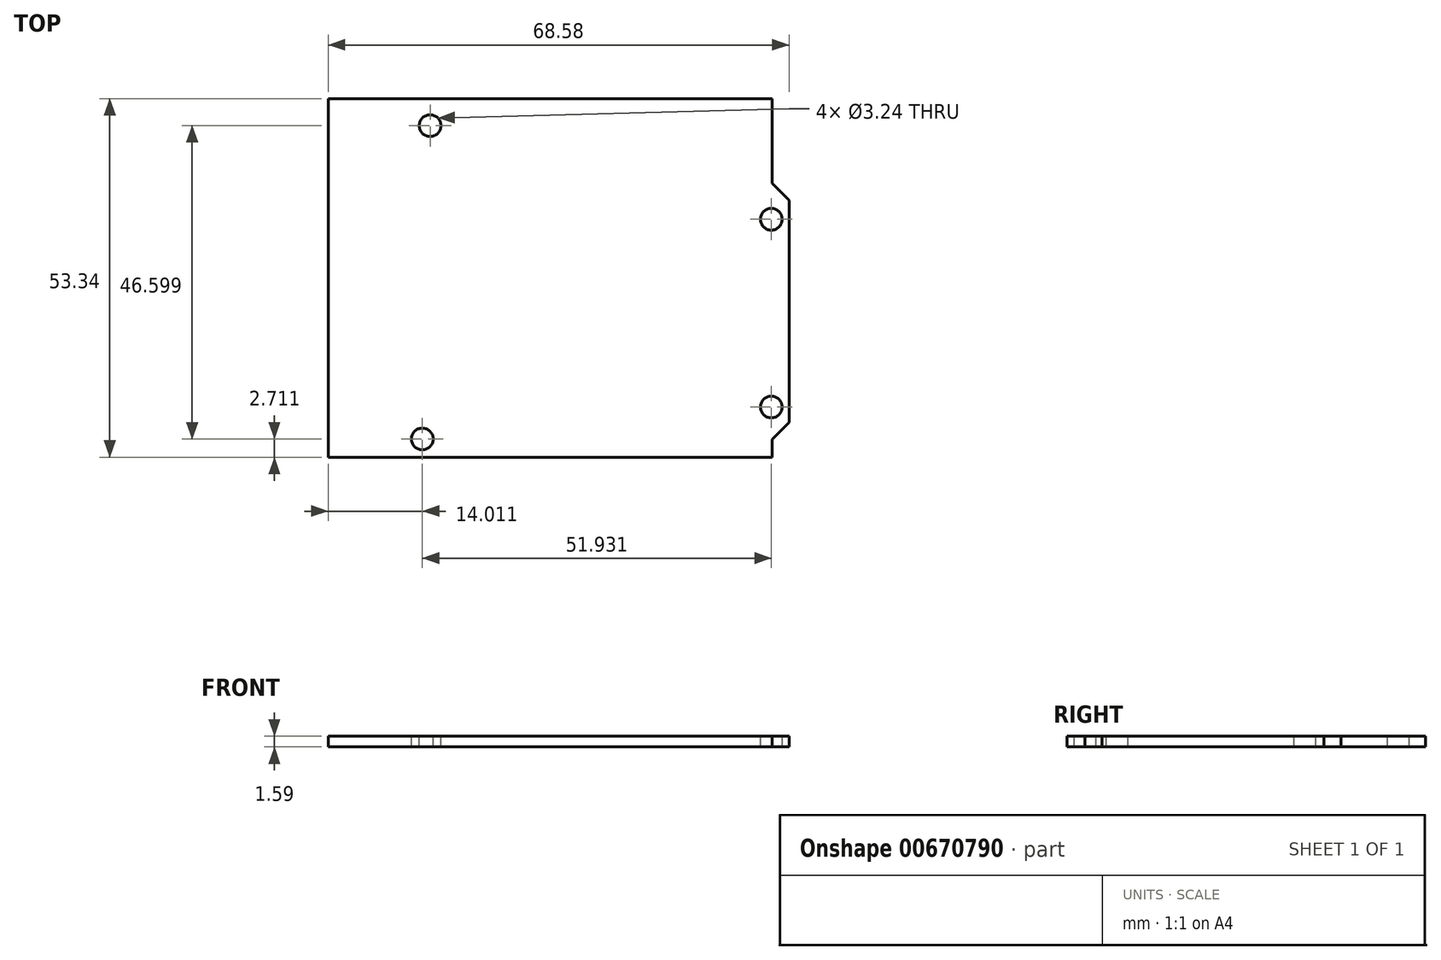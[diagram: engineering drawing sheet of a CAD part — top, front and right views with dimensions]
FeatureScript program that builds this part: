
annotation { "Feature Type Name" : "Feature", "Feature Type Description" : "" }
export const myFeature = defineFeature(function(context is Context, id is Id, definition is map)
    precondition{}
    {
        {
            var Q0;
            Q0=qCreatedBy(makeId("Top.planeOp"),FACE);
            var sketch = newSketch(context, id + "F0", { "sketchPlane" : qUnion([Q0])});
            skLineSegment(sketch, "E0", {"start": v(-34.46, 26.67) * mm, "end": v(-34.46, -26.67) * mm});
            skLineSegment(sketch, "E1", {"start": v(-34.46, -26.67) * mm, "end": v(31.58, -26.67) * mm});
            skLineSegment(sketch, "E2", {"start": v(31.58, -26.67) * mm, "end": v(31.58, 26.67) * mm});
            skLineSegment(sketch, "E3", {"start": v(31.58, 26.67) * mm, "end": v(-34.46, 26.67) * mm});
            skLineSegment(sketch, "E4", {"start": v(0, 26.67) * mm, "end": v(0, 0) * mm, "construction": true});
            skLineSegment(sketch, "E5", {"start": v(0, 0) * mm, "end": v(-34.46, 0) * mm, "construction": true});
            skLineSegment(sketch, "E6", {"start": v(31.58, -24) * mm, "end": v(34.12, -21.46) * mm});
            skLineSegment(sketch, "E7", {"start": v(34.12, -21.46) * mm, "end": v(34.12, 11.56) * mm});
            skLineSegment(sketch, "E8", {"start": v(34.12, 11.56) * mm, "end": v(31.58, 14.1) * mm});
            skSolve(sketch);
        }
        {
            var Q0;
            Q0 = qSketchRegion(id + "F0", true);
            extrude(context, id + "F1", {"entities" : qUnion([Q0]), "depth" : 1.59 * mm, "offsetDistance" : 25 * mm});
        }
        {
            var Q0;
            Q0=makeQuery(id+"F1.opExtrude","CAP_FACE",FACE,{"disambiguationData":[OSD([sQuery(id+"F0.wireOp",EDGE,"E0"),sQuery(id+"F0.wireOp",EDGE,"E1"),sQuery(id+"F0.wireOp",EDGE,"E2"),sQuery(id+"F0.wireOp",EDGE,"E3"),sQuery(id+"F0.wireOp",EDGE,"E6"),sQuery(id+"F0.wireOp",EDGE,"E7"),sQuery(id+"F0.wireOp",EDGE,"E8")])],"isStart":false});
            var sketch = newSketch(context, id + "F2", { "sketchPlane" : qUnion([Q0])});
            skCircle(sketch, "E9", {"center": v(-19.29, 22.64) * mm, "radius": 1.62 * mm});
            skCircle(sketch, "E10", {"center": v(-20.45, -23.96) * mm, "radius": 1.62 * mm});
            skCircle(sketch, "E11", {"center": v(31.48, 8.72) * mm, "radius": 1.62 * mm});
            skCircle(sketch, "E12", {"center": v(31.48, -19.2) * mm, "radius": 1.62 * mm});
            skSolve(sketch);
        }
        {
            var Q0;
            Q0 = qSketchRegion(id + "F2", true);
            extrude(context, id + "F3", {"entities" : qUnion([Q0]), "operationType" : NewBodyOperationType.REMOVE, "endBound" : BoundingType.THROUGH_ALL, "oppositeDirection" : true, "depth" : 25 * mm, "offsetDistance" : 25 * mm});
        }
    });
